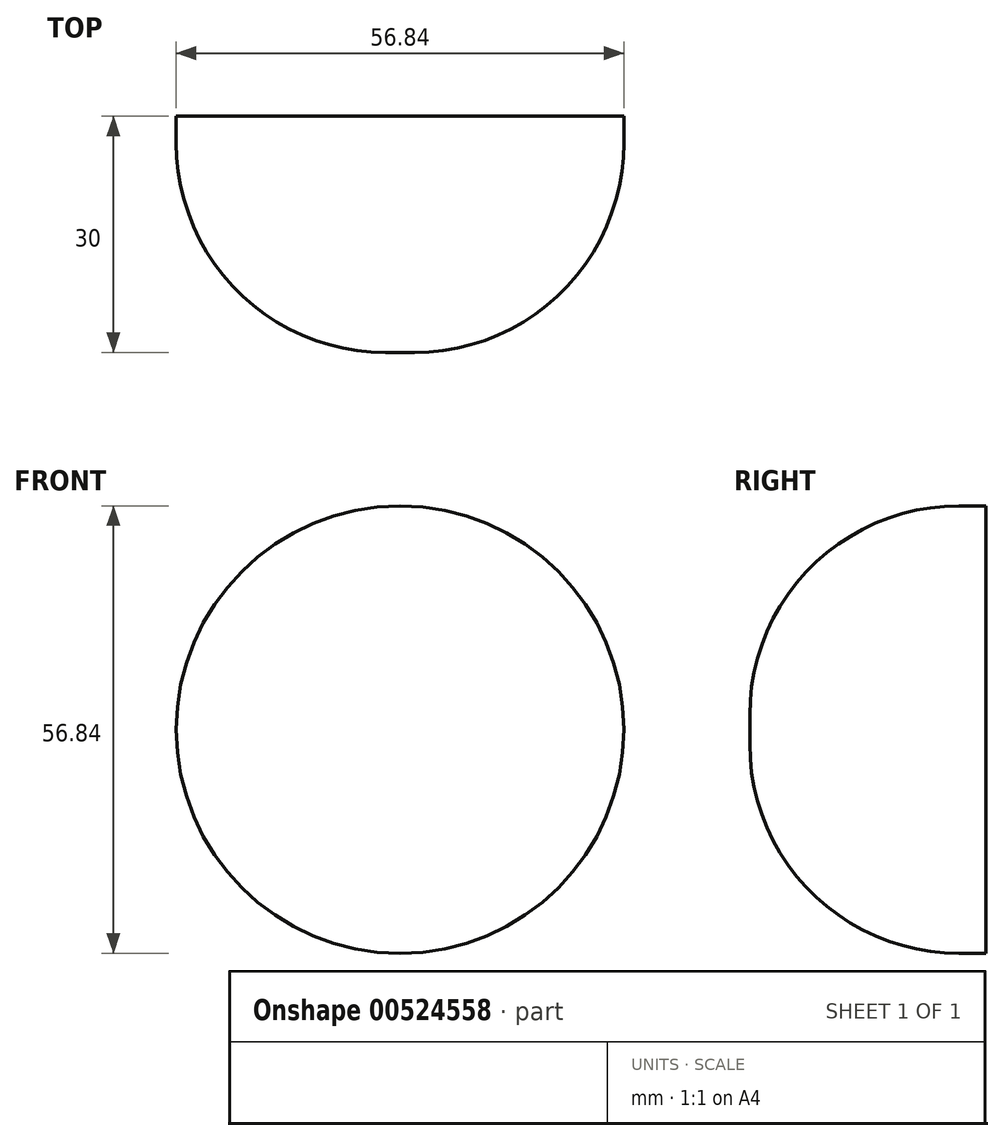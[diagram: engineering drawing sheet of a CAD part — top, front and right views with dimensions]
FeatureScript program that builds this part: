
annotation { "Feature Type Name" : "Feature", "Feature Type Description" : "" }
export const myFeature = defineFeature(function(context is Context, id is Id, definition is map)
    precondition{}
    {
        {
            var Q0;
            Q0=qCreatedBy(makeId("Front.planeOp"),FACE);
            var sketch = newSketch(context, id + "F0", { "sketchPlane" : qUnion([Q0])});
            skCircle(sketch, "E0", {"center": v(0, 0) * mm, "radius": 28.42 * mm});
            skSolve(sketch);
        }
        {
            var Q0;
            Q0=qSketchRegion(id+"F0",true);
            extrude(context, id + "F1", {"entities" : qUnion([Q0]), "depth" : 30 * mm, "offsetDistance" : 25 * mm});
        }
        {
            var Q0;
            Q0=makeQuery(id+"F1.opExtrude","CAP_EDGE",EDGE,{"disambiguationData":[OSD([sQuery(id+"F0.wireOp",EDGE,"E0")])],"isStart":false});
            fillet(context, id + "F2", {"entities" : qUnion([Q0]), "radius" : 26.56 * mm, "tangentPropagation" : true, "allowEdgeOverflow" : false});
        }
    });
